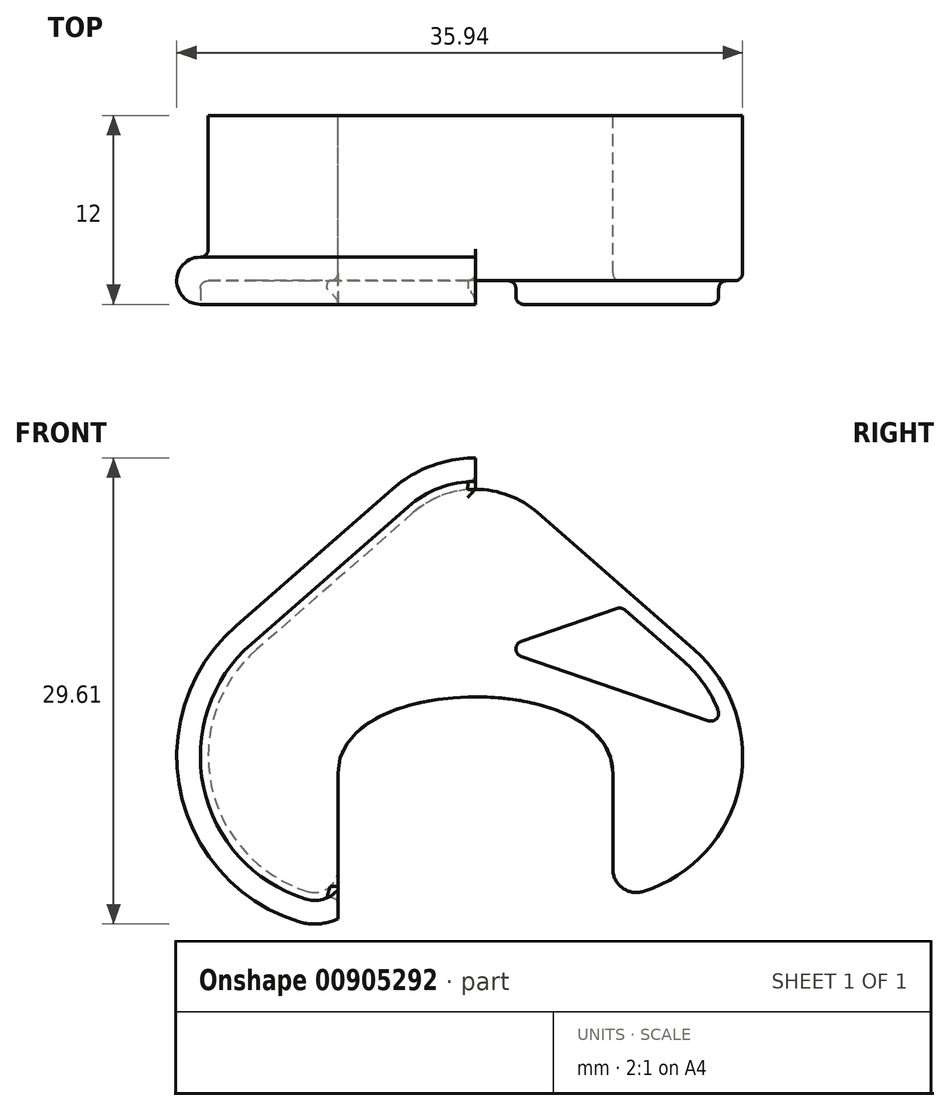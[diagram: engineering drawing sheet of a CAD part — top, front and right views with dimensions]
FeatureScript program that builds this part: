
annotation { "Feature Type Name" : "Feature", "Feature Type Description" : "" }
export const myFeature = defineFeature(function(context is Context, id is Id, definition is map)
    precondition{}
    {
        {
            var Q0;
            Q0=qCreatedBy(makeId("Front.planeOp"),FACE);
            var sketch = newSketch(context, id + "F0", { "sketchPlane" : qUnion([Q0])});
            skArc(sketch, "E0", {"start": v(-7.73, 14.72) * mm, "mid": v(-6.23, 10.16) * mm, "end": v(-2.32, 7.36) * mm});
            skArc(sketch, "E1", {"start": v(-4.88, 14.73) * mm, "mid": v(0, 9.85) * mm, "end": v(4.87, 14.72) * mm});
            skLineSegment(sketch, "E2", {"start": v(4.87, 14.72) * mm, "end": v(4.87, 15.6) * mm});
            skLineSegment(sketch, "E3", {"start": v(7.72, 14.72) * mm, "end": v(7.72, 15.6) * mm});
            skLineSegment(sketch, "E4", {"start": v(7.72, 15.6) * mm, "end": v(4.88, 15.6) * mm, "construction": true});
            skArc(sketch, "E5", {"start": v(7.72, 15.6) * mm, "mid": v(6.3, 17.01) * mm, "end": v(4.88, 15.6) * mm});
            skPoint(sketch, "E6", {"position": v(6.3, 17.02) * mm});
            skLineSegment(sketch, "E7", {"start": v(0, 0) * mm, "end": v(0, 7) * mm, "construction": true});
            skLineSegment(sketch, "E8.MirrorCS", {"start": v(-4.87, 14.72) * mm, "end": v(-4.87, 15.6) * mm});
            skLineSegment(sketch, "E9.MirrorCS", {"start": v(-7.72, 14.72) * mm, "end": v(-7.72, 15.6) * mm});
            skArc(sketch, "E10.MirrorCS", {"start": v(-7.72, 15.6) * mm, "mid": v(-6.3, 17.01) * mm, "end": v(-4.88, 15.6) * mm});
            skPoint(sketch, "E11.MirrorP", {"position": v(-6.3, 17.02) * mm});
            skLineSegment(sketch, "E12", {"start": v(-8.72, 17.52) * mm, "end": v(-8.72, 0) * mm});
            skLineSegment(sketch, "E13", {"start": v(-8.72, 0) * mm, "end": v(0, 0) * mm});
            skLineSegment(sketch, "E14.MirrorCS", {"start": v(8.72, 17.52) * mm, "end": v(8.72, 0) * mm});
            skLineSegment(sketch, "E15.MirrorCS", {"start": v(8.72, 0) * mm, "end": v(0, 0) * mm});
            skPoint(sketch, "E16", {"position": v(0, 9.85) * mm});
            skPoint(sketch, "E17", {"position": v(0, 22.35) * mm});
            skFitSpline(sketch, "E18", {"points": [v(-8.72, 17.52) * mm, v(8.72, 17.52) * mm], "startDerivative": vector(0, 19.34) * mm, "endDerivative": vector(0, -19.34) * mm});
            skPoint(sketch, "E19", {"position": v(0, 37.5) * mm});
            skLineSegment(sketch, "E20", {"start": v(0, 14.72) * mm, "end": v(-2.32, 7.36) * mm, "construction": true});
            skLineSegment(sketch, "E21", {"start": v(-25.95, 14.8) * mm, "end": v(-13.9, 25.35) * mm, "construction": true});
            skArc(sketch, "E22", {"start": v(-3.95, 34.05) * mm, "mid": v(-2.1, 35.15) * mm, "end": v(0, 35.53) * mm});
            skLineSegment(sketch, "E23", {"start": v(-13.9, 25.35) * mm, "end": v(-3.95, 34.05) * mm});
            skLineSegment(sketch, "E24", {"start": v(-3.95, 34.05) * mm, "end": v(0, 37.5) * mm, "construction": true});
            skArc(sketch, "E25", {"start": v(-2.32, 7.36) * mm, "mid": v(-1.18, 7.09) * mm, "end": v(0, 7) * mm});
            skArc(sketch, "E26", {"start": v(0, 7) * mm, "mid": v(5.46, 9.26) * mm, "end": v(7.72, 14.72) * mm});
            skLineSegment(sketch, "E27", {"start": v(-2.32, 7.36) * mm, "end": v(-10.68, 10) * mm});
            skArc(sketch, "E28", {"start": v(-13.9, 25.35) * mm, "mid": v(-16.78, 16.73) * mm, "end": v(-10.68, 10) * mm});
            skArc(sketch, "E29", {"start": v(-10.68, 10) * mm, "mid": v(-9.34, 10.21) * mm, "end": v(-8.72, 11.42) * mm});
            skLineSegment(sketch, "E30", {"start": v(-10.68, 10) * mm, "end": v(-25.95, 14.8) * mm, "construction": true});
            skArc(sketch, "E31.MirrorCS", {"start": v(10.68, 10) * mm, "mid": v(9.34, 10.21) * mm, "end": v(8.72, 11.42) * mm});
            skArc(sketch, "E32.MirrorCS", {"start": v(13.9, 25.35) * mm, "mid": v(16.78, 16.73) * mm, "end": v(10.68, 10) * mm});
            skLineSegment(sketch, "E33.MirrorCS", {"start": v(13.9, 25.35) * mm, "end": v(3.95, 34.05) * mm});
            skArc(sketch, "E34.MirrorCS", {"start": v(3.95, 34.05) * mm, "mid": v(2.1, 35.15) * mm, "end": v(0, 35.53) * mm});
            skSolve(sketch);
        }
        {
            var Q0;
            {var subQ1=sQuery(id+"F0.wireOp",EDGE,"E18");Q0=makeQuery(id+"F0.imprint","IMPRINT",FACE,{"disambiguationData":[TD([[makeQuery(id+"F0.imprint","IMPRINT",EDGE,{"derivedFrom":subQ1}),1.0]])]});}
            extrude(context, id + "F1", {"entities" : qUnion([Q0]), "depth" : 12 * mm, "offsetDistance" : 25 * mm, "symmetric" : true});
        }
        {
            var Q0;
            Q0=qCreatedBy(makeId("Right.planeOp"),FACE);
            var sketch = newSketch(context, id + "F2", { "sketchPlane" : qUnion([Q0])});
            skLineSegment(sketch, "E35", {"start": v(-6, 35.53) * mm, "end": v(6, 35.53) * mm});
            skLineSegment(sketch, "E36", {"start": v(-6, 35.53) * mm, "end": v(-6, 36.03) * mm});
            skArc(sketch, "E37", {"start": v(-6, 36.03) * mm, "mid": v(-4.5, 37.53) * mm, "end": v(-3, 36.03) * mm});
            skArc(sketch, "E38", {"start": v(-3, 36.03) * mm, "mid": v(-2.85, 35.68) * mm, "end": v(-2.5, 35.53) * mm});
            skLineSegment(sketch, "E39", {"start": v(0, 35.53) * mm, "end": v(0, 40.21) * mm, "construction": true});
            skPoint(sketch, "E40", {"position": v(-4.5, 37.53) * mm});
            skArc(sketch, "E41.MirrorCS", {"start": v(3, 36.03) * mm, "mid": v(2.85, 35.68) * mm, "end": v(2.5, 35.53) * mm});
            skArc(sketch, "E42.MirrorCS", {"start": v(6, 36.03) * mm, "mid": v(4.5, 37.53) * mm, "end": v(3, 36.03) * mm});
            skLineSegment(sketch, "E43.MirrorCS", {"start": v(6, 35.53) * mm, "end": v(6, 36.03) * mm});
            skSolve(sketch);
        }
        {
            var Q0;
            {var subQ2=sQuery(id+"F2.wireOp",EDGE,"E41.MirrorCS");Q0=makeQuery(id+"F2.imprint","IMPRINT",FACE,{"disambiguationData":[TD([[makeQuery(id+"F2.imprint","IMPRINT",EDGE,{"derivedFrom":subQ2}),1.0]])]});}
            var Q1;
            {var subQ0=sQuery(id+"F2.wireOp",EDGE,"E36");Q1=makeQuery(id+"F2.imprint","IMPRINT",FACE,{"disambiguationData":[TD([[makeQuery(id+"F2.imprint","IMPRINT",EDGE,{"derivedFrom":subQ0}),-1.0]])]});}
            var Q2;
            Q2=sQuery(id+"F0.wireOp",EDGE,"E22");
            var Q3;
            Q3=sQuery(id+"F0.wireOp",EDGE,"E23");
            var Q4;
            Q4=sQuery(id+"F0.wireOp",EDGE,"E28");
            var Q5;
            Q5=sQuery(id+"F0.wireOp",EDGE,"E29");
            sweep(context, id + "F3", {"operationType" : NewBodyOperationType.ADD, "profiles" : qUnion([Q0, Q1]), "path" : qUnion([Q2, Q3, Q4, Q5])});
        }
        {
            var Q0;
            Q0=makeQuery(id+"F0.imprint","IMPRINT",FACE,{"disambiguationData":[TD([[makeQuery(id+"F0.imprint","IMPRINT",EDGE,{"derivedFrom":sQuery(id+"F0.wireOp",EDGE,"E0")}),-1.0]])]});
            var Q1;
            Q1=makeQuery(id+"F0.imprint","IMPRINT",FACE,{"disambiguationData":[TD([[makeQuery(id+"F0.imprint","IMPRINT",EDGE,{"derivedFrom":sQuery(id+"F0.wireOp",EDGE,"E0")}),1.0]])]});
            var Q2;
            Q2=sQuery(id+"F0.wireOp",EDGE,"E13");
            revolve(context, id + "F4", {"operationType" : NewBodyOperationType.REMOVE, "surfaceOperationType" : NewSurfaceOperationType.NEW, "entities" : qUnion([Q0, Q1]), "axis" : qUnion([Q2]), "revolveType" : RevolveType.FULL, "oppositeDirection" : true});
        }
        {
            var Q0;
            {var subQ0=sQuery(id+"F2.wireOp",EDGE,"E36");var subQ1=sQuery(id+"F0.wireOp",EDGE,"E22");Q0=makeQuery(id+"FemrMwj8Leh8vnp_1.1.F3.boolean.opBoolean","MERGE",FACE,{"derivedFrom":[makeQuery(id+"F3.boolean.opBoolean","MERGE",FACE,{"derivedFrom":[makeQuery(id+"F1.opExtrude","CAP_FACE",FACE,{"disambiguationData":[OSD([sQuery(id+"F0.wireOp",EDGE,"E12"),sQuery(id+"F0.wireOp",EDGE,"E14.MirrorCS"),sQuery(id+"F0.wireOp",EDGE,"E18"),subQ1,sQuery(id+"F0.wireOp",EDGE,"E23"),sQuery(id+"F0.wireOp",EDGE,"E28"),sQuery(id+"F0.wireOp",EDGE,"E29"),sQuery(id+"F0.wireOp",EDGE,"E31.MirrorCS"),sQuery(id+"F0.wireOp",EDGE,"E32.MirrorCS"),sQuery(id+"F0.wireOp",EDGE,"E33.MirrorCS"),sQuery(id+"F0.wireOp",EDGE,"E34.MirrorCS")])],"isStart":false}),makeQuery(id+"F3.opSweep","SWEPT_FACE",FACE,{"disambiguationData":[OSD([subQ1,subQ0])]})]}),makeQuery(id+"FemrMwj8Leh8vnp_1.1.F3.opSweep","SWEPT_FACE",FACE,{"disambiguationData":[OSD([subQ1,subQ0])]})]});}
            var sketch = newSketch(context, id + "F5", { "sketchPlane" : qUnion([Q0])});
            skArc(sketch, "E44.0", {"start": v(14.22, 25.73) * mm, "mid": v(17.27, 16.63) * mm, "end": v(10.83, 9.51) * mm});
            skLineSegment(sketch, "E44.1", {"start": v(-4.28, 34.42) * mm, "end": v(-14.22, 25.73) * mm});
            skArc(sketch, "E44.2", {"start": v(4.28, 34.42) * mm, "mid": v(0, 36.03) * mm, "end": v(-4.28, 34.42) * mm});
            skLineSegment(sketch, "E44.3", {"start": v(8.72, 17.52) * mm, "end": v(8.72, 10.1) * mm});
            skArc(sketch, "E44.4", {"start": v(-14.22, 25.73) * mm, "mid": v(-17.27, 16.63) * mm, "end": v(-10.83, 9.51) * mm});
            skLineSegment(sketch, "E44.5", {"start": v(4.28, 34.42) * mm, "end": v(14.22, 25.73) * mm});
            skLineSegment(sketch, "E44.6", {"start": v(-8.72, 17.52) * mm, "end": v(-8.72, 10.1) * mm});
            skFitSpline(sketch, "E44.7", {"points": [v(-8.72, 17.52) * mm, v(-8.72, 23.96) * mm, v(8.72, 23.96) * mm, v(8.72, 17.52) * mm]});
            skArc(sketch, "E45.0", {"start": v(-13.24, 24.6) * mm, "mid": v(-15.96, 18.16) * mm, "end": v(-12.6, 12.04) * mm});
            skArc(sketch, "E45.1", {"start": v(13.24, 24.6) * mm, "mid": v(15.96, 18.16) * mm, "end": v(12.6, 12.04) * mm});
            skLineSegment(sketch, "E45.2", {"start": v(3.3, 33.3) * mm, "end": v(13.24, 24.6) * mm});
            skArc(sketch, "E45.3", {"start": v(3.3, 33.3) * mm, "mid": v(0, 34.53) * mm, "end": v(-3.3, 33.3) * mm});
            skLineSegment(sketch, "E45.4", {"start": v(-3.3, 33.3) * mm, "end": v(-13.24, 24.6) * mm});
            skLineSegment(sketch, "E46.0", {"start": v(-10.22, 17.52) * mm, "end": v(-10.22, 13.27) * mm});
            skFitSpline(sketch, "E46.1", {"points": [v(-10.22, 17.52) * mm, v(-10.22, 18.09) * mm, v(-10.03, 19.2) * mm, v(-9.2, 20.61) * mm, v(-8.06, 21.7) * mm, v(-6.69, 22.52) * mm, v(-5.16, 23.13) * mm, v(-2.96, 23.69) * mm, v(0, 23.96) * mm, v(2.96, 23.69) * mm, v(5.16, 23.13) * mm, v(6.69, 22.52) * mm, v(8.06, 21.7) * mm, v(9.2, 20.61) * mm, v(10.03, 19.2) * mm, v(10.22, 18.09) * mm, v(10.22, 17.52) * mm]});
            skLineSegment(sketch, "E46.2", {"start": v(10.22, 17.52) * mm, "end": v(10.22, 13.27) * mm});
            skArc(sketch, "E47.filletArc", {"start": v(-12.6, 12.04) * mm, "mid": v(-11.04, 11.94) * mm, "end": v(-10.22, 13.27) * mm});
            skArc(sketch, "E48.filletArc", {"start": v(10.22, 13.27) * mm, "mid": v(11.04, 11.94) * mm, "end": v(12.6, 12.04) * mm});
            skArc(sketch, "E49.0", {"start": v(-10.83, 9.51) * mm, "mid": v(-9.69, 9.5) * mm, "end": v(-8.72, 10.1) * mm});
            skArc(sketch, "E49.1", {"start": v(10.83, 9.51) * mm, "mid": v(9.69, 9.5) * mm, "end": v(8.72, 10.1) * mm});
            skLineSegment(sketch, "E50", {"start": v(-14.22, 25.73) * mm, "end": v(-20.9, 19.9) * mm, "construction": true});
            skLineSegment(sketch, "E51", {"start": v(-20.9, 19.9) * mm, "end": v(-15.54, 12.83) * mm, "construction": true});
            skLineSegment(sketch, "E52", {"start": v(-19.55, 21.06) * mm, "end": v(-19.82, 18.48) * mm, "construction": true});
            skLineSegment(sketch, "E53", {"start": v(-20.9, 19.9) * mm, "end": v(-15.93, 19.39) * mm, "construction": true});
            skPoint(sketch, "E54.orphan", {"position": v(-19.69, 19.77) * mm});
            skLineSegment(sketch, "E55", {"start": v(-15.93, 19.39) * mm, "end": v(9.27, 28.06) * mm});
            skLineSegment(sketch, "E56.MirrorCS", {"start": v(-15.93, 19.39) * mm, "end": v(-10.22, 16) * mm});
            skLineSegment(sketch, "E57.0", {"start": v(-16.27, 18.43) * mm, "end": v(-10.22, 14.85) * mm});
            skLineSegment(sketch, "E58.0", {"start": v(-16.25, 20.33) * mm, "end": v(8.4, 28.82) * mm});
            skLineSegment(sketch, "E59", {"start": v(0, 0) * mm, "end": v(0, 18.02) * mm, "construction": true});
            skLineSegment(sketch, "E60.MirrorCS", {"start": v(16.27, 18.43) * mm, "end": v(10.22, 14.85) * mm});
            skLineSegment(sketch, "E61.MirrorCS", {"start": v(15.93, 19.39) * mm, "end": v(10.22, 16) * mm});
            skLineSegment(sketch, "E62.MirrorCS", {"start": v(15.93, 19.39) * mm, "end": v(-9.27, 28.06) * mm});
            skLineSegment(sketch, "E63.MirrorCS", {"start": v(16.25, 20.33) * mm, "end": v(-8.4, 28.82) * mm});
            skSolve(sketch);
        }
        {
            var Q0;
            {var subQ0=sQuery(id+"F2.wireOp",EDGE,"E36");var subQ1=sQuery(id+"F0.wireOp",EDGE,"E22");Q0=makeQuery(id+"FemrMwj8Leh8vnp_1.1.F3.boolean.opBoolean","MERGE",FACE,{"derivedFrom":[makeQuery(id+"F3.boolean.opBoolean","MERGE",FACE,{"derivedFrom":[makeQuery(id+"F1.opExtrude","CAP_FACE",FACE,{"disambiguationData":[OSD([sQuery(id+"F0.wireOp",EDGE,"E12"),sQuery(id+"F0.wireOp",EDGE,"E14.MirrorCS"),sQuery(id+"F0.wireOp",EDGE,"E18"),subQ1,sQuery(id+"F0.wireOp",EDGE,"E23"),sQuery(id+"F0.wireOp",EDGE,"E28"),sQuery(id+"F0.wireOp",EDGE,"E29"),sQuery(id+"F0.wireOp",EDGE,"E31.MirrorCS"),sQuery(id+"F0.wireOp",EDGE,"E32.MirrorCS"),sQuery(id+"F0.wireOp",EDGE,"E33.MirrorCS"),sQuery(id+"F0.wireOp",EDGE,"E34.MirrorCS")])],"isStart":false}),makeQuery(id+"F3.opSweep","SWEPT_FACE",FACE,{"disambiguationData":[OSD([subQ1,subQ0])]})]}),makeQuery(id+"FemrMwj8Leh8vnp_1.1.F3.opSweep","SWEPT_FACE",FACE,{"disambiguationData":[OSD([subQ1,subQ0])]})]});}
            var sketch = newSketch(context, id + "F6", { "sketchPlane" : qUnion([Q0])});
            skLineSegment(sketch, "E64.0", {"start": v(-15, 18.84) * mm, "end": v(-10.98, 16.46) * mm});
            skArc(sketch, "E64.1", {"start": v(13.24, 24.6) * mm, "mid": v(14.51, 23.18) * mm, "end": v(15.42, 21.5) * mm});
            skLineSegment(sketch, "E64.2", {"start": v(10.22, 17.52) * mm, "end": v(10.22, 16.89) * mm});
            skArc(sketch, "E64.3", {"start": v(3.3, 33.3) * mm, "mid": v(0, 34.53) * mm, "end": v(-3.3, 33.3) * mm});
            skLineSegment(sketch, "E64.4", {"start": v(-14.9, 19.74) * mm, "end": v(-9.5, 21.6) * mm});
            skLineSegment(sketch, "E64.5", {"start": v(14.9, 19.74) * mm, "end": v(9.5, 21.6) * mm});
            skLineSegment(sketch, "E64.6", {"start": v(15, 18.84) * mm, "end": v(10.98, 16.46) * mm});
            skArc(sketch, "E64.7", {"start": v(-13.24, 24.6) * mm, "mid": v(-14.51, 23.18) * mm, "end": v(-15.42, 21.5) * mm});
            skFitSpline(sketch, "E64.8", {"points": [v(-10.22, 17.52) * mm, v(-10.22, 18.09) * mm, v(-10.03, 19.2) * mm, v(-9.2, 20.61) * mm, v(-8.06, 21.7) * mm, v(-6.69, 22.52) * mm, v(-5.16, 23.13) * mm, v(-2.96, 23.69) * mm, v(0, 23.96) * mm, v(2.96, 23.69) * mm, v(5.16, 23.13) * mm, v(6.69, 22.52) * mm, v(8.06, 21.7) * mm, v(9.2, 20.61) * mm, v(10.03, 19.2) * mm, v(10.22, 18.09) * mm, v(10.22, 17.52) * mm]});
            skLineSegment(sketch, "E64.9", {"start": v(3.3, 33.3) * mm, "end": v(7.76, 29.39) * mm});
            skLineSegment(sketch, "E64.10", {"start": v(14.8, 20.84) * mm, "end": v(2.91, 24.92) * mm});
            skLineSegment(sketch, "E64.11", {"start": v(-14.8, 20.84) * mm, "end": v(-2.91, 24.92) * mm});
            skLineSegment(sketch, "E64.12", {"start": v(-3.3, 33.3) * mm, "end": v(-7.76, 29.39) * mm});
            skLineSegment(sketch, "E64.13", {"start": v(15.1, 17.74) * mm, "end": v(10.47, 15) * mm});
            skArc(sketch, "E64.14", {"start": v(10.22, 13.27) * mm, "mid": v(11.04, 11.94) * mm, "end": v(12.6, 12.04) * mm});
            skLineSegment(sketch, "E64.15", {"start": v(-15.1, 17.74) * mm, "end": v(-10.47, 15) * mm});
            skLineSegment(sketch, "E64.16", {"start": v(-10.22, 17.52) * mm, "end": v(-10.22, 16.89) * mm});
            skLineSegment(sketch, "E65", {"start": v(-9.5, 27.87) * mm, "end": v(-13.24, 24.6) * mm});
            skLineSegment(sketch, "E66", {"start": v(9.5, 27.87) * mm, "end": v(13.24, 24.6) * mm});
            skLineSegment(sketch, "E67", {"start": v(-2.91, 25.87) * mm, "end": v(-9, 27.97) * mm});
            skLineSegment(sketch, "E68", {"start": v(-1.54, 25.4) * mm, "end": v(0, 25.93) * mm, "construction": true});
            skLineSegment(sketch, "E69", {"start": v(0.16, 25.98) * mm, "end": v(7.6, 28.54) * mm});
            skLineSegment(sketch, "E70", {"start": v(-0.16, 25.98) * mm, "end": v(-7.6, 28.54) * mm});
            skLineSegment(sketch, "E71", {"start": v(2.91, 25.87) * mm, "end": v(9, 27.97) * mm});
            skLineSegment(sketch, "E72", {"start": v(1.54, 25.4) * mm, "end": v(0, 25.93) * mm, "construction": true});
            skLineSegment(sketch, "E73", {"start": v(0, 24.87) * mm, "end": v(-1.54, 25.4) * mm, "construction": true});
            skLineSegment(sketch, "E74", {"start": v(0, 24.87) * mm, "end": v(1.54, 25.4) * mm, "construction": true});
            skArc(sketch, "E75", {"start": v(-15.73, 20.51) * mm, "mid": v(-15.85, 19.95) * mm, "end": v(-15.93, 19.39) * mm});
            skArc(sketch, "E76", {"start": v(-15.93, 19.39) * mm, "mid": v(-15.97, 18.73) * mm, "end": v(-15.95, 18.08) * mm});
            skArc(sketch, "E77", {"start": v(-15.85, 17.22) * mm, "mid": v(-14.74, 14.3) * mm, "end": v(-12.6, 12.04) * mm});
            skLineSegment(sketch, "E78", {"start": v(-10.22, 14.56) * mm, "end": v(-10.22, 13.27) * mm});
            skLineSegment(sketch, "E79", {"start": v(-10.22, 16) * mm, "end": v(-10.22, 14.85) * mm});
            skLineSegment(sketch, "E80", {"start": v(-5.4, 23.01) * mm, "end": v(0, 24.87) * mm, "construction": true});
            skFitSpline(sketch, "E81", {"points": [v(-10.22, 17.52) * mm, v(-10.22, 18.09) * mm, v(-10.03, 19.2) * mm, v(-9.2, 20.61) * mm, v(-8.06, 21.7) * mm, v(-6.69, 22.52) * mm, v(-5.16, 23.13) * mm, v(-2.96, 23.69) * mm, v(0, 23.96) * mm, v(2.96, 23.69) * mm, v(5.16, 23.13) * mm, v(6.69, 22.52) * mm, v(8.06, 21.7) * mm, v(9.2, 20.61) * mm, v(10.03, 19.2) * mm, v(10.22, 18.09) * mm, v(10.22, 17.52) * mm]});
            skArc(sketch, "E82", {"start": v(15.73, 20.51) * mm, "mid": v(15.85, 19.95) * mm, "end": v(15.93, 19.39) * mm});
            skArc(sketch, "E83", {"start": v(15.93, 19.39) * mm, "mid": v(15.97, 18.73) * mm, "end": v(15.95, 18.08) * mm});
            skArc(sketch, "E84", {"start": v(15.85, 17.22) * mm, "mid": v(14.74, 14.3) * mm, "end": v(12.6, 12.04) * mm});
            skLineSegment(sketch, "E85", {"start": v(10.22, 14.56) * mm, "end": v(10.22, 13.27) * mm});
            skLineSegment(sketch, "E86", {"start": v(10.22, 16) * mm, "end": v(10.22, 14.85) * mm});
            skPoint(sketch, "E87.visualSharp", {"position": v(10.22, 14.85) * mm});
            skArc(sketch, "E87.filletArc", {"start": v(10.47, 15) * mm, "mid": v(10.3, 14.8) * mm, "end": v(10.22, 14.56) * mm});
            skPoint(sketch, "E88.newPointA", {"position": v(16.27, 18.43) * mm});
            skArc(sketch, "E88.filletArc", {"start": v(15.85, 17.22) * mm, "mid": v(15.65, 17.72) * mm, "end": v(15.1, 17.74) * mm});
            skPoint(sketch, "E89.visualSharp", {"position": v(15.93, 19.39) * mm});
            skArc(sketch, "E89.filletArc", {"start": v(15, 18.84) * mm, "mid": v(15.24, 19.32) * mm, "end": v(14.9, 19.74) * mm});
            skPoint(sketch, "E90.visualSharp", {"position": v(10.22, 16) * mm});
            skArc(sketch, "E90.filletArc", {"start": v(10.22, 16.89) * mm, "mid": v(10.48, 16.45) * mm, "end": v(10.98, 16.46) * mm});
            skArc(sketch, "E91.filletArc", {"start": v(9.5, 21.6) * mm, "mid": v(8.91, 21.4) * mm, "end": v(8.95, 20.8) * mm});
            skPoint(sketch, "E92.newPointA", {"position": v(16.25, 20.33) * mm});
            skArc(sketch, "E92.filletArc", {"start": v(14.8, 20.84) * mm, "mid": v(15.31, 20.96) * mm, "end": v(15.42, 21.5) * mm});
            skPoint(sketch, "E93.newPointA", {"position": v(9.27, 28.06) * mm});
            skArc(sketch, "E93.filletArc", {"start": v(9.5, 27.87) * mm, "mid": v(9.26, 27.98) * mm, "end": v(9, 27.97) * mm});
            skPoint(sketch, "E94.visualSharp", {"position": v(1.54, 25.4) * mm});
            skArc(sketch, "E94.filletArc", {"start": v(2.91, 25.87) * mm, "mid": v(2.57, 25.4) * mm, "end": v(2.91, 24.92) * mm});
            skPoint(sketch, "E95.visualSharp", {"position": v(8.4, 28.82) * mm});
            skArc(sketch, "E95.filletArc", {"start": v(7.6, 28.54) * mm, "mid": v(7.92, 28.92) * mm, "end": v(7.76, 29.39) * mm});
            skPoint(sketch, "E96.visualSharp", {"position": v(0, 25.93) * mm});
            skArc(sketch, "E96.filletArc", {"start": v(-0.16, 25.98) * mm, "mid": v(0, 25.95) * mm, "end": v(0.16, 25.98) * mm});
            skPoint(sketch, "E97.visualSharp", {"position": v(-8.4, 28.82) * mm});
            skArc(sketch, "E97.filletArc", {"start": v(-7.76, 29.39) * mm, "mid": v(-7.92, 28.92) * mm, "end": v(-7.6, 28.54) * mm});
            skPoint(sketch, "E98.visualSharp", {"position": v(-1.54, 25.4) * mm});
            skArc(sketch, "E98.filletArc", {"start": v(-2.91, 24.92) * mm, "mid": v(-2.57, 25.4) * mm, "end": v(-2.91, 25.87) * mm});
            skPoint(sketch, "E99.newPointA", {"position": v(-16.25, 20.33) * mm});
            skArc(sketch, "E99.filletArc", {"start": v(-15.42, 21.5) * mm, "mid": v(-15.31, 20.96) * mm, "end": v(-14.8, 20.84) * mm});
            skPoint(sketch, "E100.visualSharp", {"position": v(-15.93, 19.39) * mm});
            skArc(sketch, "E100.filletArc", {"start": v(-14.9, 19.74) * mm, "mid": v(-15.24, 19.32) * mm, "end": v(-15, 18.84) * mm});
            skPoint(sketch, "E101.newPointA", {"position": v(-16.27, 18.43) * mm});
            skArc(sketch, "E101.filletArc", {"start": v(-15.1, 17.74) * mm, "mid": v(-15.65, 17.72) * mm, "end": v(-15.85, 17.22) * mm});
            skPoint(sketch, "E102.visualSharp", {"position": v(-10.22, 14.85) * mm});
            skArc(sketch, "E102.filletArc", {"start": v(-10.22, 14.56) * mm, "mid": v(-10.3, 14.8) * mm, "end": v(-10.47, 15) * mm});
            skPoint(sketch, "E103.visualSharp", {"position": v(-10.22, 16) * mm});
            skArc(sketch, "E103.filletArc", {"start": v(-10.98, 16.46) * mm, "mid": v(-10.48, 16.45) * mm, "end": v(-10.22, 16.89) * mm});
            skArc(sketch, "E104.0", {"start": v(-12.6, 12.04) * mm, "mid": v(-11.04, 11.94) * mm, "end": v(-10.22, 13.27) * mm});
            skArc(sketch, "E105.filletArc", {"start": v(-8.95, 20.8) * mm, "mid": v(-8.91, 21.4) * mm, "end": v(-9.5, 21.6) * mm});
            skPoint(sketch, "E106.newPointA", {"position": v(-9.27, 28.06) * mm});
            skArc(sketch, "E106.filletArc", {"start": v(-9, 27.97) * mm, "mid": v(-9.26, 27.98) * mm, "end": v(-9.5, 27.87) * mm});
            skSolve(sketch);
        }
        {
            var Q0;
            Q0=makeQuery(id+"F6.imprint","IMPRINT",FACE,{"disambiguationData":[TD([[makeQuery(id+"F6.imprint","IMPRINT",EDGE,{"derivedFrom":sQuery(id+"F6.wireOp",EDGE,"E64.3")}),1.0]])]});
            var Q1;
            Q1=makeQuery(id+"F6.imprint","IMPRINT",FACE,{"disambiguationData":[TD([[makeQuery(id+"F6.imprint","IMPRINT",EDGE,{"derivedFrom":sQuery(id+"F6.wireOp",EDGE,"E64.7")}),1.0]])]});
            var Q2;
            Q2=makeQuery(id+"F6.imprint","IMPRINT",FACE,{"disambiguationData":[TD([[makeQuery(id+"F6.imprint","IMPRINT",EDGE,{"derivedFrom":sQuery(id+"F6.wireOp",EDGE,"E64.15")}),-1.0]])]});
            var Q3;
            Q3=makeQuery(id+"F6.imprint","IMPRINT",FACE,{"disambiguationData":[TD([[makeQuery(id+"F6.imprint","IMPRINT",EDGE,{"derivedFrom":sQuery(id+"F6.wireOp",EDGE,"E64.0")}),1.0]])]});
            var Q4;
            Q4=makeQuery(id+"F6.imprint","IMPRINT",FACE,{"disambiguationData":[TD([[makeQuery(id+"F6.imprint","IMPRINT",EDGE,{"derivedFrom":sQuery(id+"F6.wireOp",EDGE,"E64.2")}),1.0]])]});
            var Q5;
            Q5=makeQuery(id+"F6.imprint","IMPRINT",FACE,{"disambiguationData":[TD([[makeQuery(id+"F6.imprint","IMPRINT",EDGE,{"derivedFrom":sQuery(id+"F6.wireOp",EDGE,"E64.13")}),1.0]])]});
            var Q6;
            Q6=makeQuery(id+"F6.imprint","IMPRINT",FACE,{"disambiguationData":[TD([[makeQuery(id+"F6.imprint","IMPRINT",EDGE,{"derivedFrom":sQuery(id+"F6.wireOp",EDGE,"E64.1")}),-1.0]])]});
            extrude(context, id + "F7", {"entities" : qUnion([Q0, Q1, Q2, Q3, Q4, Q5, Q6]), "operationType" : NewBodyOperationType.REMOVE, "oppositeDirection" : true, "depth" : 1.5 * mm, "offsetDistance" : 25 * mm});
        }
        {
            var Q0;
            {var subQ0=sQuery(id+"F2.wireOp",EDGE,"E36");var subQ1=sQuery(id+"F0.wireOp",EDGE,"E22");Q0=makeQuery(id+"FemrMwj8Leh8vnp_1.1.F3.boolean.opBoolean","MERGE",FACE,{"derivedFrom":[makeQuery(id+"F3.boolean.opBoolean","MERGE",FACE,{"derivedFrom":[makeQuery(id+"F1.opExtrude","CAP_FACE",FACE,{"disambiguationData":[OSD([sQuery(id+"F0.wireOp",EDGE,"E12"),sQuery(id+"F0.wireOp",EDGE,"E14.MirrorCS"),sQuery(id+"F0.wireOp",EDGE,"E18"),subQ1,sQuery(id+"F0.wireOp",EDGE,"E23"),sQuery(id+"F0.wireOp",EDGE,"E28"),sQuery(id+"F0.wireOp",EDGE,"E29"),sQuery(id+"F0.wireOp",EDGE,"E31.MirrorCS"),sQuery(id+"F0.wireOp",EDGE,"E32.MirrorCS"),sQuery(id+"F0.wireOp",EDGE,"E33.MirrorCS"),sQuery(id+"F0.wireOp",EDGE,"E34.MirrorCS")])],"isStart":false}),makeQuery(id+"F3.opSweep","SWEPT_FACE",FACE,{"disambiguationData":[OSD([subQ1,subQ0])]})]}),makeQuery(id+"FemrMwj8Leh8vnp_1.1.F3.opSweep","SWEPT_FACE",FACE,{"disambiguationData":[OSD([subQ1,subQ0])]})]});}
            var Q1;
            {var subQ0=sQuery(id+"F2.wireOp",EDGE,"E43.MirrorCS");var subQ1=sQuery(id+"F0.wireOp",EDGE,"E22");Q1=makeQuery(id+"FemrMwj8Leh8vnp_1.1.F3.boolean.opBoolean","MERGE",FACE,{"derivedFrom":[makeQuery(id+"F3.boolean.opBoolean","MERGE",FACE,{"derivedFrom":[makeQuery(id+"F1.opExtrude","CAP_FACE",FACE,{"disambiguationData":[OSD([sQuery(id+"F0.wireOp",EDGE,"E12"),sQuery(id+"F0.wireOp",EDGE,"E14.MirrorCS"),sQuery(id+"F0.wireOp",EDGE,"E18"),subQ1,sQuery(id+"F0.wireOp",EDGE,"E23"),sQuery(id+"F0.wireOp",EDGE,"E28"),sQuery(id+"F0.wireOp",EDGE,"E29"),sQuery(id+"F0.wireOp",EDGE,"E31.MirrorCS"),sQuery(id+"F0.wireOp",EDGE,"E32.MirrorCS"),sQuery(id+"F0.wireOp",EDGE,"E33.MirrorCS"),sQuery(id+"F0.wireOp",EDGE,"E34.MirrorCS")])],"isStart":true}),makeQuery(id+"F3.opSweep","SWEPT_FACE",FACE,{"disambiguationData":[OSD([subQ1,subQ0])]})]}),makeQuery(id+"FemrMwj8Leh8vnp_1.1.F3.opSweep","SWEPT_FACE",FACE,{"disambiguationData":[OSD([subQ1,subQ0])]})]});}
            var Q2;
            Q2=makeQuery(id+"Fz0XMLnkfh5b9sZ_1.1.F7.boolean.opBoolean","COPY",FACE,{"derivedFrom":makeQuery(id+"Fz0XMLnkfh5b9sZ_1.1.F7.opExtrude","CAP_FACE",FACE,{"disambiguationData":[OSD([sQuery(id+"F6.wireOp",EDGE,"E64.3"),sQuery(id+"F6.wireOp",EDGE,"E64.9"),sQuery(id+"F6.wireOp",EDGE,"E64.12"),sQuery(id+"F6.wireOp",EDGE,"E69"),sQuery(id+"F6.wireOp",EDGE,"E70"),sQuery(id+"F6.wireOp",EDGE,"E95.filletArc"),sQuery(id+"F6.wireOp",EDGE,"E96.filletArc"),sQuery(id+"F6.wireOp",EDGE,"E97.filletArc")])],"isStart":false})});
            var Q3;
            Q3=makeQuery(id+"Fz0XMLnkfh5b9sZ_1.1.F7.boolean.opBoolean","COPY",FACE,{"derivedFrom":makeQuery(id+"Fz0XMLnkfh5b9sZ_1.1.F7.opExtrude","CAP_FACE",FACE,{"disambiguationData":[OSD([sQuery(id+"F6.wireOp",EDGE,"E64.7"),sQuery(id+"F6.wireOp",EDGE,"E64.11"),sQuery(id+"F6.wireOp",EDGE,"E65"),sQuery(id+"F6.wireOp",EDGE,"E67"),sQuery(id+"F6.wireOp",EDGE,"E98.filletArc"),sQuery(id+"F6.wireOp",EDGE,"E99.filletArc"),sQuery(id+"F6.wireOp",EDGE,"E106.filletArc")])],"isStart":false})});
            var Q4;
            Q4=makeQuery(id+"Fz0XMLnkfh5b9sZ_1.1.F7.boolean.opBoolean","COPY",FACE,{"derivedFrom":makeQuery(id+"Fz0XMLnkfh5b9sZ_1.1.F7.opExtrude","CAP_FACE",FACE,{"disambiguationData":[OSD([sQuery(id+"F6.wireOp",EDGE,"E64.1"),sQuery(id+"F6.wireOp",EDGE,"E64.10"),sQuery(id+"F6.wireOp",EDGE,"E66"),sQuery(id+"F6.wireOp",EDGE,"E71"),sQuery(id+"F6.wireOp",EDGE,"E92.filletArc"),sQuery(id+"F6.wireOp",EDGE,"E93.filletArc"),sQuery(id+"F6.wireOp",EDGE,"E94.filletArc")])],"isStart":false})});
            var Q5;
            Q5=makeQuery(id+"Fz0XMLnkfh5b9sZ_1.1.F7.boolean.opBoolean","COPY",FACE,{"derivedFrom":makeQuery(id+"Fz0XMLnkfh5b9sZ_1.1.F7.opExtrude","CAP_FACE",FACE,{"disambiguationData":[OSD([sQuery(id+"F6.wireOp",EDGE,"E64.0"),sQuery(id+"F6.wireOp",EDGE,"E64.4"),sQuery(id+"F6.wireOp",EDGE,"E64.8"),sQuery(id+"F6.wireOp",EDGE,"E64.16"),sQuery(id+"F6.wireOp",EDGE,"E100.filletArc"),sQuery(id+"F6.wireOp",EDGE,"E103.filletArc"),sQuery(id+"F6.wireOp",EDGE,"E105.filletArc")])],"isStart":false})});
            var Q6;
            Q6=makeQuery(id+"Fz0XMLnkfh5b9sZ_1.1.F7.boolean.opBoolean","COPY",FACE,{"derivedFrom":makeQuery(id+"Fz0XMLnkfh5b9sZ_1.1.F7.opExtrude","CAP_FACE",FACE,{"disambiguationData":[OSD([sQuery(id+"F6.wireOp",EDGE,"E64.15"),sQuery(id+"F6.wireOp",EDGE,"E77"),sQuery(id+"F6.wireOp",EDGE,"E78"),sQuery(id+"F6.wireOp",EDGE,"E101.filletArc"),sQuery(id+"F6.wireOp",EDGE,"E102.filletArc"),sQuery(id+"F6.wireOp",EDGE,"E104.0")])],"isStart":false})});
            var Q7;
            Q7=makeQuery(id+"Fz0XMLnkfh5b9sZ_1.1.F7.boolean.opBoolean","COPY",FACE,{"derivedFrom":makeQuery(id+"Fz0XMLnkfh5b9sZ_1.1.F7.opExtrude","CAP_FACE",FACE,{"disambiguationData":[OSD([sQuery(id+"F6.wireOp",EDGE,"E64.13"),sQuery(id+"F6.wireOp",EDGE,"E64.14"),sQuery(id+"F6.wireOp",EDGE,"E84"),sQuery(id+"F6.wireOp",EDGE,"E85"),sQuery(id+"F6.wireOp",EDGE,"E87.filletArc"),sQuery(id+"F6.wireOp",EDGE,"E88.filletArc")])],"isStart":false})});
            var Q8;
            Q8=makeQuery(id+"Fz0XMLnkfh5b9sZ_1.1.F7.boolean.opBoolean","COPY",FACE,{"derivedFrom":makeQuery(id+"Fz0XMLnkfh5b9sZ_1.1.F7.opExtrude","CAP_FACE",FACE,{"disambiguationData":[OSD([sQuery(id+"F6.wireOp",EDGE,"E64.2"),sQuery(id+"F6.wireOp",EDGE,"E64.5"),sQuery(id+"F6.wireOp",EDGE,"E64.6"),sQuery(id+"F6.wireOp",EDGE,"E81"),sQuery(id+"F6.wireOp",EDGE,"E89.filletArc"),sQuery(id+"F6.wireOp",EDGE,"E90.filletArc"),sQuery(id+"F6.wireOp",EDGE,"E91.filletArc")])],"isStart":false})});
            var Q9;
            Q9=makeQuery(id+"F7.boolean.opBoolean","COPY",FACE,{"derivedFrom":makeQuery(id+"F7.opExtrude","CAP_FACE",FACE,{"disambiguationData":[OSD([sQuery(id+"F6.wireOp",EDGE,"E64.1"),sQuery(id+"F6.wireOp",EDGE,"E64.10"),sQuery(id+"F6.wireOp",EDGE,"E66"),sQuery(id+"F6.wireOp",EDGE,"E71"),sQuery(id+"F6.wireOp",EDGE,"E92.filletArc"),sQuery(id+"F6.wireOp",EDGE,"E93.filletArc"),sQuery(id+"F6.wireOp",EDGE,"E94.filletArc")])],"isStart":false})});
            var Q10;
            Q10=makeQuery(id+"F7.boolean.opBoolean","COPY",FACE,{"derivedFrom":makeQuery(id+"F7.opExtrude","CAP_FACE",FACE,{"disambiguationData":[OSD([sQuery(id+"F6.wireOp",EDGE,"E64.3"),sQuery(id+"F6.wireOp",EDGE,"E64.9"),sQuery(id+"F6.wireOp",EDGE,"E64.12"),sQuery(id+"F6.wireOp",EDGE,"E69"),sQuery(id+"F6.wireOp",EDGE,"E70"),sQuery(id+"F6.wireOp",EDGE,"E95.filletArc"),sQuery(id+"F6.wireOp",EDGE,"E96.filletArc"),sQuery(id+"F6.wireOp",EDGE,"E97.filletArc")])],"isStart":false})});
            var Q11;
            Q11=makeQuery(id+"F7.boolean.opBoolean","COPY",FACE,{"derivedFrom":makeQuery(id+"F7.opExtrude","CAP_FACE",FACE,{"disambiguationData":[OSD([sQuery(id+"F6.wireOp",EDGE,"E64.7"),sQuery(id+"F6.wireOp",EDGE,"E64.11"),sQuery(id+"F6.wireOp",EDGE,"E65"),sQuery(id+"F6.wireOp",EDGE,"E67"),sQuery(id+"F6.wireOp",EDGE,"E98.filletArc"),sQuery(id+"F6.wireOp",EDGE,"E99.filletArc"),sQuery(id+"F6.wireOp",EDGE,"E106.filletArc")])],"isStart":false})});
            var Q12;
            Q12=makeQuery(id+"F7.boolean.opBoolean","COPY",FACE,{"derivedFrom":makeQuery(id+"F7.opExtrude","CAP_FACE",FACE,{"disambiguationData":[OSD([sQuery(id+"F6.wireOp",EDGE,"E64.2"),sQuery(id+"F6.wireOp",EDGE,"E64.5"),sQuery(id+"F6.wireOp",EDGE,"E64.6"),sQuery(id+"F6.wireOp",EDGE,"E81"),sQuery(id+"F6.wireOp",EDGE,"E89.filletArc"),sQuery(id+"F6.wireOp",EDGE,"E90.filletArc"),sQuery(id+"F6.wireOp",EDGE,"E91.filletArc")])],"isStart":false})});
            var Q13;
            Q13=makeQuery(id+"F7.boolean.opBoolean","COPY",FACE,{"derivedFrom":makeQuery(id+"F7.opExtrude","CAP_FACE",FACE,{"disambiguationData":[OSD([sQuery(id+"F6.wireOp",EDGE,"E64.0"),sQuery(id+"F6.wireOp",EDGE,"E64.4"),sQuery(id+"F6.wireOp",EDGE,"E64.8"),sQuery(id+"F6.wireOp",EDGE,"E64.16"),sQuery(id+"F6.wireOp",EDGE,"E100.filletArc"),sQuery(id+"F6.wireOp",EDGE,"E103.filletArc"),sQuery(id+"F6.wireOp",EDGE,"E105.filletArc")])],"isStart":false})});
            var Q14;
            Q14=makeQuery(id+"F7.boolean.opBoolean","COPY",FACE,{"derivedFrom":makeQuery(id+"F7.opExtrude","CAP_FACE",FACE,{"disambiguationData":[OSD([sQuery(id+"F6.wireOp",EDGE,"E64.15"),sQuery(id+"F6.wireOp",EDGE,"E77"),sQuery(id+"F6.wireOp",EDGE,"E78"),sQuery(id+"F6.wireOp",EDGE,"E101.filletArc"),sQuery(id+"F6.wireOp",EDGE,"E102.filletArc"),sQuery(id+"F6.wireOp",EDGE,"E104.0")])],"isStart":false})});
            var Q15;
            Q15=makeQuery(id+"F7.boolean.opBoolean","COPY",FACE,{"derivedFrom":makeQuery(id+"F7.opExtrude","CAP_FACE",FACE,{"disambiguationData":[OSD([sQuery(id+"F6.wireOp",EDGE,"E64.13"),sQuery(id+"F6.wireOp",EDGE,"E64.14"),sQuery(id+"F6.wireOp",EDGE,"E84"),sQuery(id+"F6.wireOp",EDGE,"E85"),sQuery(id+"F6.wireOp",EDGE,"E87.filletArc"),sQuery(id+"F6.wireOp",EDGE,"E88.filletArc")])],"isStart":false})});
            fillet(context, id + "F8", {"entities" : qUnion([Q0, Q1, Q2, Q3, Q4, Q5, Q6, Q7, Q8, Q9, Q10, Q11, Q12, Q13, Q14, Q15]), "radius" : .5 * mm, "tangentPropagation" : true, "allowEdgeOverflow" : false});
        }
    });
